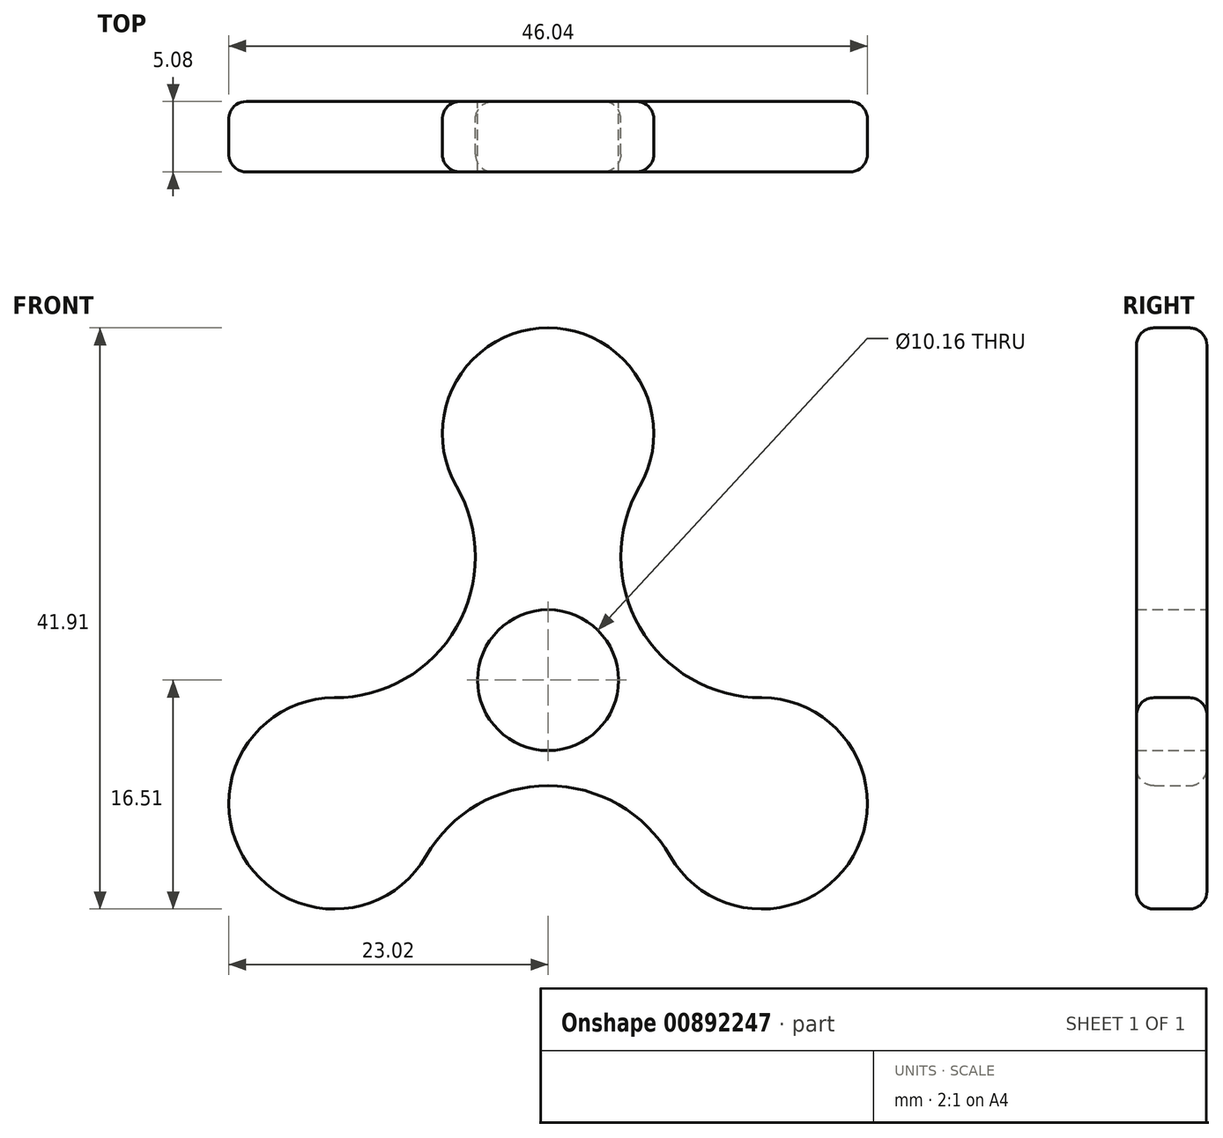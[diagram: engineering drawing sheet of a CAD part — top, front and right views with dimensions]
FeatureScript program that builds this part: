
annotation { "Feature Type Name" : "Feature", "Feature Type Description" : "" }
export const myFeature = defineFeature(function(context is Context, id is Id, definition is map)
    precondition{}
    {
        {
            var Q0;
            Q0=qCreatedBy(makeId("Front.planeOp"),FACE);
            var sketch = newSketch(context, id + "F0", { "sketchPlane" : qUnion([Q0])});
            skCircle(sketch, "E0", {"center": v(0, 0) * mm, "radius": 25.4 * mm});
            skPoint(sketch, "E1", {"position": v(0, 25.4) * mm});
            skPoint(sketch, "E2", {"position": v(-22, -12.7) * mm});
            skPoint(sketch, "E3", {"position": v(22, -12.7) * mm});
            skLineSegment(sketch, "E4", {"start": v(0, 25.4) * mm, "end": v(0, 0) * mm});
            skLineSegment(sketch, "E5", {"start": v(0, 0) * mm, "end": v(22, -12.7) * mm});
            skLineSegment(sketch, "E6", {"start": v(0, 0) * mm, "end": v(-22, -12.7) * mm});
            skCircle(sketch, "E7", {"center": v(0, 17.78) * mm, "radius": 7.62 * mm});
            skCircle(sketch, "E8", {"center": v(-15.4, -8.89) * mm, "radius": 7.62 * mm});
            skCircle(sketch, "E9", {"center": v(15.4, -8.89) * mm, "radius": 7.62 * mm});
            skCircle(sketch, "E10", {"center": v(0, 0) * mm, "radius": 7.62 * mm});
            skCircle(sketch, "E11", {"center": v(-10.78, 8.9) * mm, "radius": 6.35 * mm});
            skCircle(sketch, "E12", {"center": v(-13.09, 4.89) * mm, "radius": 6.35 * mm});
            skCircle(sketch, "E13", {"center": v(-2.31, -13.78) * mm, "radius": 6.35 * mm});
            skCircle(sketch, "E14", {"center": v(2.31, -13.78) * mm, "radius": 6.35 * mm});
            skCircle(sketch, "E15", {"center": v(13.09, 4.89) * mm, "radius": 6.35 * mm});
            skCircle(sketch, "E16", {"center": v(10.78, 8.9) * mm, "radius": 6.35 * mm});
            skCircle(sketch, "E17", {"center": v(0, 0) * mm, "radius": 5.08 * mm});
            skCircle(sketch, "E18", {"center": v(-15.4, 8.9) * mm, "radius": 10.16 * mm});
            skCircle(sketch, "E19", {"center": v(15.4, 8.9) * mm, "radius": 10.16 * mm});
            skCircle(sketch, "E20", {"center": v(0, -17.78) * mm, "radius": 10.16 * mm});
            skSolve(sketch);
        }
        {
            var Q0;
            {var subQ0=sQuery(id+"F0.wireOp",EDGE,"E7");var subQ1=sQuery(id+"F0.wireOp",EDGE,"E4");var subQ3=makeQuery(id+"F0.imprint","INTERSECT",VERTEX,{"derivedFrom":[subQ1,subQ0]});Q0=makeQuery(id+"F0.imprint","IMPRINT",FACE,{"disambiguationData":[TD([[makeQuery(id+"F0.imprint","IMPRINT",EDGE,{"disambiguationData":[TD([[subQ3,-1.0]])],"derivedFrom":subQ0}),1.0]])]});}
            var Q1;
            {var subQ0=sQuery(id+"F0.wireOp",EDGE,"E7");var subQ1=sQuery(id+"F0.wireOp",EDGE,"E4");var subQ3=makeQuery(id+"F0.imprint","INTERSECT",VERTEX,{"derivedFrom":[subQ1,subQ0]});Q1=makeQuery(id+"F0.imprint","IMPRINT",FACE,{"disambiguationData":[TD([[makeQuery(id+"F0.imprint","IMPRINT",EDGE,{"disambiguationData":[TD([[subQ3,1.0]])],"derivedFrom":subQ0}),1.0]])]});}
            var Q2;
            {var subQ0=sQuery(id+"F0.wireOp",EDGE,"E7");var subQ1=sQuery(id+"F0.wireOp",EDGE,"E4");var subQ2=makeQuery(id+"F0.imprint","INTERSECT",VERTEX,{"derivedFrom":[subQ1,subQ0]});Q2=makeQuery(id+"F0.imprint","IMPRINT",FACE,{"disambiguationData":[TD([[makeQuery(id+"F0.imprint","IMPRINT",EDGE,{"disambiguationData":[TD([[subQ2,-1.0]])],"derivedFrom":subQ1}),-1.0]])]});}
            var Q3;
            {var subQ0=sQuery(id+"F0.wireOp",EDGE,"E7");var subQ1=sQuery(id+"F0.wireOp",EDGE,"E4");var subQ2=makeQuery(id+"F0.imprint","INTERSECT",VERTEX,{"derivedFrom":[subQ1,subQ0]});Q3=makeQuery(id+"F0.imprint","IMPRINT",FACE,{"disambiguationData":[TD([[makeQuery(id+"F0.imprint","IMPRINT",EDGE,{"disambiguationData":[TD([[subQ2,-1.0]])],"derivedFrom":subQ1}),1.0]])]});}
            var Q4;
            {var subQ0=sQuery(id+"F0.wireOp",EDGE,"E10");var subQ1=sQuery(id+"F0.wireOp",EDGE,"E6");var subQ2=makeQuery(id+"F0.imprint","INTERSECT",VERTEX,{"derivedFrom":[subQ1,subQ0]});Q4=makeQuery(id+"F0.imprint","IMPRINT",FACE,{"disambiguationData":[TD([[makeQuery(id+"F0.imprint","IMPRINT",EDGE,{"disambiguationData":[TD([[subQ2,-1.0]])],"derivedFrom":subQ1}),-1.0]])]});}
            var Q5;
            {var subQ0=sQuery(id+"F0.wireOp",EDGE,"E10");var subQ1=sQuery(id+"F0.wireOp",EDGE,"E6");var subQ2=makeQuery(id+"F0.imprint","INTERSECT",VERTEX,{"derivedFrom":[subQ1,subQ0]});Q5=makeQuery(id+"F0.imprint","IMPRINT",FACE,{"disambiguationData":[TD([[makeQuery(id+"F0.imprint","IMPRINT",EDGE,{"disambiguationData":[TD([[subQ2,-1.0]])],"derivedFrom":subQ1}),1.0]])]});}
            var Q6;
            {var subQ0=sQuery(id+"F0.wireOp",EDGE,"E8");var subQ1=sQuery(id+"F0.wireOp",EDGE,"E6");var subQ3=makeQuery(id+"F0.imprint","INTERSECT",VERTEX,{"derivedFrom":[subQ1,subQ0]});Q6=makeQuery(id+"F0.imprint","IMPRINT",FACE,{"disambiguationData":[TD([[makeQuery(id+"F0.imprint","IMPRINT",EDGE,{"disambiguationData":[TD([[subQ3,-1.0]])],"derivedFrom":subQ0}),1.0]])]});}
            var Q7;
            {var subQ0=sQuery(id+"F0.wireOp",EDGE,"E8");var subQ1=sQuery(id+"F0.wireOp",EDGE,"E6");var subQ3=makeQuery(id+"F0.imprint","INTERSECT",VERTEX,{"derivedFrom":[subQ1,subQ0]});Q7=makeQuery(id+"F0.imprint","IMPRINT",FACE,{"disambiguationData":[TD([[makeQuery(id+"F0.imprint","IMPRINT",EDGE,{"disambiguationData":[TD([[subQ3,1.0]])],"derivedFrom":subQ0}),1.0]])]});}
            var Q8;
            {var subQ0=sQuery(id+"F0.wireOp",EDGE,"E10");var subQ3=sQuery(id+"F0.wireOp",EDGE,"E6");var subQ4=makeQuery(id+"F0.imprint","INTERSECT",VERTEX,{"derivedFrom":[subQ3,subQ0]});Q8=makeQuery(id+"F0.imprint","IMPRINT",FACE,{"disambiguationData":[TD([[makeQuery(id+"F0.imprint","IMPRINT",EDGE,{"disambiguationData":[TD([[subQ4,-1.0]])],"derivedFrom":subQ0}),1.0]])]});}
            var Q9;
            {var subQ0=sQuery(id+"F0.wireOp",EDGE,"E10");var subQ4=sQuery(id+"F0.wireOp",EDGE,"E4");var subQ6=makeQuery(id+"F0.imprint","INTERSECT",VERTEX,{"derivedFrom":[subQ4,subQ0]});Q9=makeQuery(id+"F0.imprint","IMPRINT",FACE,{"disambiguationData":[TD([[makeQuery(id+"F0.imprint","IMPRINT",EDGE,{"disambiguationData":[TD([[subQ6,-1.0]])],"derivedFrom":subQ0}),1.0]])]});}
            var Q10;
            {var subQ0=sQuery(id+"F0.wireOp",EDGE,"E10");var subQ1=sQuery(id+"F0.wireOp",EDGE,"E5");var subQ2=makeQuery(id+"F0.imprint","INTERSECT",VERTEX,{"derivedFrom":[subQ1,subQ0]});Q10=makeQuery(id+"F0.imprint","IMPRINT",FACE,{"disambiguationData":[TD([[makeQuery(id+"F0.imprint","IMPRINT",EDGE,{"disambiguationData":[TD([[subQ2,-1.0]])],"derivedFrom":subQ1}),-1.0]])]});}
            var Q11;
            {var subQ0=sQuery(id+"F0.wireOp",EDGE,"E10");var subQ1=sQuery(id+"F0.wireOp",EDGE,"E5");var subQ2=makeQuery(id+"F0.imprint","INTERSECT",VERTEX,{"derivedFrom":[subQ1,subQ0]});Q11=makeQuery(id+"F0.imprint","IMPRINT",FACE,{"disambiguationData":[TD([[makeQuery(id+"F0.imprint","IMPRINT",EDGE,{"disambiguationData":[TD([[subQ2,-1.0]])],"derivedFrom":subQ1}),1.0]])]});}
            var Q12;
            {var subQ0=sQuery(id+"F0.wireOp",EDGE,"E9");var subQ1=sQuery(id+"F0.wireOp",EDGE,"E5");var subQ3=makeQuery(id+"F0.imprint","INTERSECT",VERTEX,{"derivedFrom":[subQ1,subQ0]});Q12=makeQuery(id+"F0.imprint","IMPRINT",FACE,{"disambiguationData":[TD([[makeQuery(id+"F0.imprint","IMPRINT",EDGE,{"disambiguationData":[TD([[subQ3,1.0]])],"derivedFrom":subQ0}),1.0]])]});}
            var Q13;
            {var subQ0=sQuery(id+"F0.wireOp",EDGE,"E9");var subQ1=sQuery(id+"F0.wireOp",EDGE,"E5");var subQ3=makeQuery(id+"F0.imprint","INTERSECT",VERTEX,{"derivedFrom":[subQ1,subQ0]});Q13=makeQuery(id+"F0.imprint","IMPRINT",FACE,{"disambiguationData":[TD([[makeQuery(id+"F0.imprint","IMPRINT",EDGE,{"disambiguationData":[TD([[subQ3,-1.0]])],"derivedFrom":subQ0}),1.0]])]});}
            var Q14;
            {var subQ0=sQuery(id+"F0.wireOp",EDGE,"jwab9ZdJ-cZyV-ynDp-2DS0-X9y9Y4CfVrNN");Q14=makeQuery(id+"F0.imprint","IMPRINT",FACE,{"disambiguationData":[TD([[makeQuery(id+"F0.imprint","IMPRINT",EDGE,{"derivedFrom":subQ0}),-1.0]])]});}
            var Q15;
            {var subQ0=sQuery(id+"F0.wireOp",EDGE,"E12");var subQ1=makeQuery(id+"F0.imprint","INTERSECT",VERTEX,{"derivedFrom":[sQuery(id+"F0.wireOp",EDGE,"E8"),subQ0]});Q15=makeQuery(id+"F0.imprint","IMPRINT",FACE,{"disambiguationData":[TD([[makeQuery(id+"F0.imprint","IMPRINT",EDGE,{"disambiguationData":[TD([[subQ1,1.0]])],"derivedFrom":subQ0}),1.0]])]});}
            var Q16;
            {var subQ0=sQuery(id+"F0.wireOp",EDGE,"E10");var subQ8=sQuery(id+"F0.wireOp",EDGE,"E4");var subQ9=makeQuery(id+"F0.imprint","INTERSECT",VERTEX,{"derivedFrom":[subQ8,subQ0]});Q16=makeQuery(id+"F0.imprint","IMPRINT",FACE,{"disambiguationData":[TD([[makeQuery(id+"F0.imprint","IMPRINT",EDGE,{"disambiguationData":[TD([[subQ9,-1.0]])],"derivedFrom":subQ8}),1.0]])]});}
            var Q17;
            {var subQ0=sQuery(id+"F0.wireOp",EDGE,"E13");var subQ1=makeQuery(id+"F0.imprint","INTERSECT",VERTEX,{"derivedFrom":[sQuery(id+"F0.wireOp",EDGE,"E10"),subQ0]});Q17=makeQuery(id+"F0.imprint","IMPRINT",FACE,{"disambiguationData":[TD([[makeQuery(id+"F0.imprint","IMPRINT",EDGE,{"disambiguationData":[TD([[subQ1,1.0]])],"derivedFrom":subQ0}),1.0]])]});}
            var Q18;
            {var subQ0=sQuery(id+"F0.wireOp",EDGE,"E14");var subQ1=makeQuery(id+"F0.imprint","INTERSECT",VERTEX,{"derivedFrom":[sQuery(id+"F0.wireOp",EDGE,"E9"),subQ0]});Q18=makeQuery(id+"F0.imprint","IMPRINT",FACE,{"disambiguationData":[TD([[makeQuery(id+"F0.imprint","IMPRINT",EDGE,{"disambiguationData":[TD([[subQ1,1.0]])],"derivedFrom":subQ0}),1.0]])]});}
            var Q19;
            {var subQ0=sQuery(id+"F0.wireOp",EDGE,"E15");var subQ1=makeQuery(id+"F0.imprint","INTERSECT",VERTEX,{"derivedFrom":[sQuery(id+"F0.wireOp",EDGE,"E10"),subQ0]});Q19=makeQuery(id+"F0.imprint","IMPRINT",FACE,{"disambiguationData":[TD([[makeQuery(id+"F0.imprint","IMPRINT",EDGE,{"disambiguationData":[TD([[subQ1,1.0]])],"derivedFrom":subQ0}),1.0]])]});}
            var Q20;
            {var subQ0=sQuery(id+"F0.wireOp",EDGE,"E16");var subQ1=makeQuery(id+"F0.imprint","INTERSECT",VERTEX,{"derivedFrom":[sQuery(id+"F0.wireOp",EDGE,"E7"),subQ0]});Q20=makeQuery(id+"F0.imprint","IMPRINT",FACE,{"disambiguationData":[TD([[makeQuery(id+"F0.imprint","IMPRINT",EDGE,{"disambiguationData":[TD([[subQ1,1.0]])],"derivedFrom":subQ0}),1.0]])]});}
            var Q21;
            {var subQ0=sQuery(id+"F0.wireOp",EDGE,"E11");var subQ1=makeQuery(id+"F0.imprint","INTERSECT",VERTEX,{"derivedFrom":[sQuery(id+"F0.wireOp",EDGE,"E7"),subQ0]});Q21=makeQuery(id+"F0.imprint","IMPRINT",FACE,{"disambiguationData":[TD([[makeQuery(id+"F0.imprint","IMPRINT",EDGE,{"disambiguationData":[TD([[subQ1,-1.0]])],"derivedFrom":subQ0}),1.0]])]});}
            var Q22;
            {var subQ0=sQuery(id+"F0.wireOp",EDGE,"E20");var subQ1=sQuery(id+"F0.wireOp",EDGE,"E8");var subQ2=makeQuery(id+"F0.imprint","INTERSECT",VERTEX,{"derivedFrom":[subQ1,subQ0]});Q22=makeQuery(id+"F0.imprint","IMPRINT",FACE,{"disambiguationData":[TD([[makeQuery(id+"F0.imprint","IMPRINT",EDGE,{"disambiguationData":[TD([[subQ2,-1.0]])],"derivedFrom":subQ1}),-1.0]])]});}
            var Q23;
            {var subQ0=sQuery(id+"F0.wireOp",EDGE,"E13");var subQ1=sQuery(id+"F0.wireOp",EDGE,"E10");var subQ2=makeQuery(id+"F0.imprint","INTERSECT",VERTEX,{"derivedFrom":[subQ1,subQ0]});Q23=makeQuery(id+"F0.imprint","IMPRINT",FACE,{"disambiguationData":[TD([[makeQuery(id+"F0.imprint","IMPRINT",EDGE,{"disambiguationData":[TD([[subQ2,-1.0]])],"derivedFrom":subQ1}),-1.0]])]});}
            var Q24;
            {var subQ0=sQuery(id+"F0.wireOp",EDGE,"E20");var subQ1=sQuery(id+"F0.wireOp",EDGE,"E10");var subQ2=makeQuery(id+"F0.imprint","INTERSECT",VERTEX,{"derivedFrom":[subQ1,subQ0]});Q24=makeQuery(id+"F0.imprint","IMPRINT",FACE,{"disambiguationData":[TD([[makeQuery(id+"F0.imprint","IMPRINT",EDGE,{"disambiguationData":[TD([[subQ2,-1.0]])],"derivedFrom":subQ1}),-1.0]])]});}
            var Q25;
            {var subQ0=sQuery(id+"F0.wireOp",EDGE,"E12");var subQ1=sQuery(id+"F0.wireOp",EDGE,"E8");var subQ2=makeQuery(id+"F0.imprint","INTERSECT",VERTEX,{"derivedFrom":[subQ1,subQ0]});Q25=makeQuery(id+"F0.imprint","IMPRINT",FACE,{"disambiguationData":[TD([[makeQuery(id+"F0.imprint","IMPRINT",EDGE,{"disambiguationData":[TD([[subQ2,-1.0]])],"derivedFrom":subQ1}),-1.0]])]});}
            var Q26;
            {var subQ0=sQuery(id+"F0.wireOp",EDGE,"E18");var subQ1=sQuery(id+"F0.wireOp",EDGE,"E10");var subQ2=makeQuery(id+"F0.imprint","INTERSECT",VERTEX,{"derivedFrom":[subQ1,subQ0]});Q26=makeQuery(id+"F0.imprint","IMPRINT",FACE,{"disambiguationData":[TD([[makeQuery(id+"F0.imprint","IMPRINT",EDGE,{"disambiguationData":[TD([[subQ2,-1.0]])],"derivedFrom":subQ1}),-1.0]])]});}
            var Q27;
            {var subQ0=sQuery(id+"F0.wireOp",EDGE,"E11");var subQ1=sQuery(id+"F0.wireOp",EDGE,"E10");var subQ2=makeQuery(id+"F0.imprint","INTERSECT",VERTEX,{"derivedFrom":[subQ1,subQ0]});Q27=makeQuery(id+"F0.imprint","IMPRINT",FACE,{"disambiguationData":[TD([[makeQuery(id+"F0.imprint","IMPRINT",EDGE,{"disambiguationData":[TD([[subQ2,-1.0]])],"derivedFrom":subQ1}),-1.0]])]});}
            var Q28;
            {var subQ0=sQuery(id+"F0.wireOp",EDGE,"E18");var subQ1=sQuery(id+"F0.wireOp",EDGE,"E7");var subQ2=makeQuery(id+"F0.imprint","INTERSECT",VERTEX,{"derivedFrom":[subQ1,subQ0]});Q28=makeQuery(id+"F0.imprint","IMPRINT",FACE,{"disambiguationData":[TD([[makeQuery(id+"F0.imprint","IMPRINT",EDGE,{"disambiguationData":[TD([[subQ2,-1.0]])],"derivedFrom":subQ1}),-1.0]])]});}
            var Q29;
            {var subQ0=sQuery(id+"F0.wireOp",EDGE,"E16");var subQ1=sQuery(id+"F0.wireOp",EDGE,"E7");var subQ2=makeQuery(id+"F0.imprint","INTERSECT",VERTEX,{"derivedFrom":[subQ1,subQ0]});Q29=makeQuery(id+"F0.imprint","IMPRINT",FACE,{"disambiguationData":[TD([[makeQuery(id+"F0.imprint","IMPRINT",EDGE,{"disambiguationData":[TD([[subQ2,-1.0]])],"derivedFrom":subQ1}),-1.0]])]});}
            var Q30;
            {var subQ0=sQuery(id+"F0.wireOp",EDGE,"E19");var subQ1=sQuery(id+"F0.wireOp",EDGE,"E10");var subQ2=makeQuery(id+"F0.imprint","INTERSECT",VERTEX,{"derivedFrom":[subQ1,subQ0]});Q30=makeQuery(id+"F0.imprint","IMPRINT",FACE,{"disambiguationData":[TD([[makeQuery(id+"F0.imprint","IMPRINT",EDGE,{"disambiguationData":[TD([[subQ2,-1.0]])],"derivedFrom":subQ1}),-1.0]])]});}
            var Q31;
            {var subQ0=sQuery(id+"F0.wireOp",EDGE,"E19");var subQ1=sQuery(id+"F0.wireOp",EDGE,"E10");var subQ2=makeQuery(id+"F0.imprint","INTERSECT",VERTEX,{"derivedFrom":[subQ1,subQ0]});Q31=makeQuery(id+"F0.imprint","IMPRINT",FACE,{"disambiguationData":[TD([[makeQuery(id+"F0.imprint","IMPRINT",EDGE,{"disambiguationData":[TD([[subQ2,1.0]])],"derivedFrom":subQ1}),-1.0]])]});}
            var Q32;
            {var subQ0=sQuery(id+"F0.wireOp",EDGE,"E15");var subQ1=sQuery(id+"F0.wireOp",EDGE,"E9");var subQ2=makeQuery(id+"F0.imprint","INTERSECT",VERTEX,{"derivedFrom":[subQ1,subQ0]});Q32=makeQuery(id+"F0.imprint","IMPRINT",FACE,{"disambiguationData":[TD([[makeQuery(id+"F0.imprint","IMPRINT",EDGE,{"disambiguationData":[TD([[subQ2,1.0]])],"derivedFrom":subQ1}),-1.0]])]});}
            var Q33;
            {var subQ0=sQuery(id+"F0.wireOp",EDGE,"E14");var subQ1=sQuery(id+"F0.wireOp",EDGE,"E9");var subQ2=makeQuery(id+"F0.imprint","INTERSECT",VERTEX,{"derivedFrom":[subQ1,subQ0]});Q33=makeQuery(id+"F0.imprint","IMPRINT",FACE,{"disambiguationData":[TD([[makeQuery(id+"F0.imprint","IMPRINT",EDGE,{"disambiguationData":[TD([[subQ2,-1.0]])],"derivedFrom":subQ1}),-1.0]])]});}
            extrude(context, id + "F1", {"entities" : qUnion([Q0, Q1, Q2, Q3, Q4, Q5, Q6, Q7, Q8, Q9, Q10, Q11, Q12, Q13, Q14, Q15, Q16, Q17, Q18, Q19, Q20, Q21, Q22, Q23, Q24, Q25, Q26, Q27, Q28, Q29, Q30, Q31, Q32, Q33]), "endBound" : BoundingType.SYMMETRIC, "depth" : 5.08 * mm, "offsetDistance" : 25.4 * mm});
        }
        {
            var Q0;
            Q0=makeQuery(id+"F1.opExtrude","CAP_EDGE",EDGE,{"disambiguationData":[OSD([sQuery(id+"F0.wireOp",EDGE,"E20")])],"isStart":true});
            var Q1;
            Q1=makeQuery(id+"F1.opExtrude","CAP_EDGE",EDGE,{"disambiguationData":[OSD([sQuery(id+"F0.wireOp",EDGE,"E19")])],"isStart":false});
            fillet(context, id + "F2", {"entities" : qUnion([Q0, Q1]), "radius" : 1.27 * mm, "tangentPropagation" : true, "allowEdgeOverflow" : false});
        }
    });
